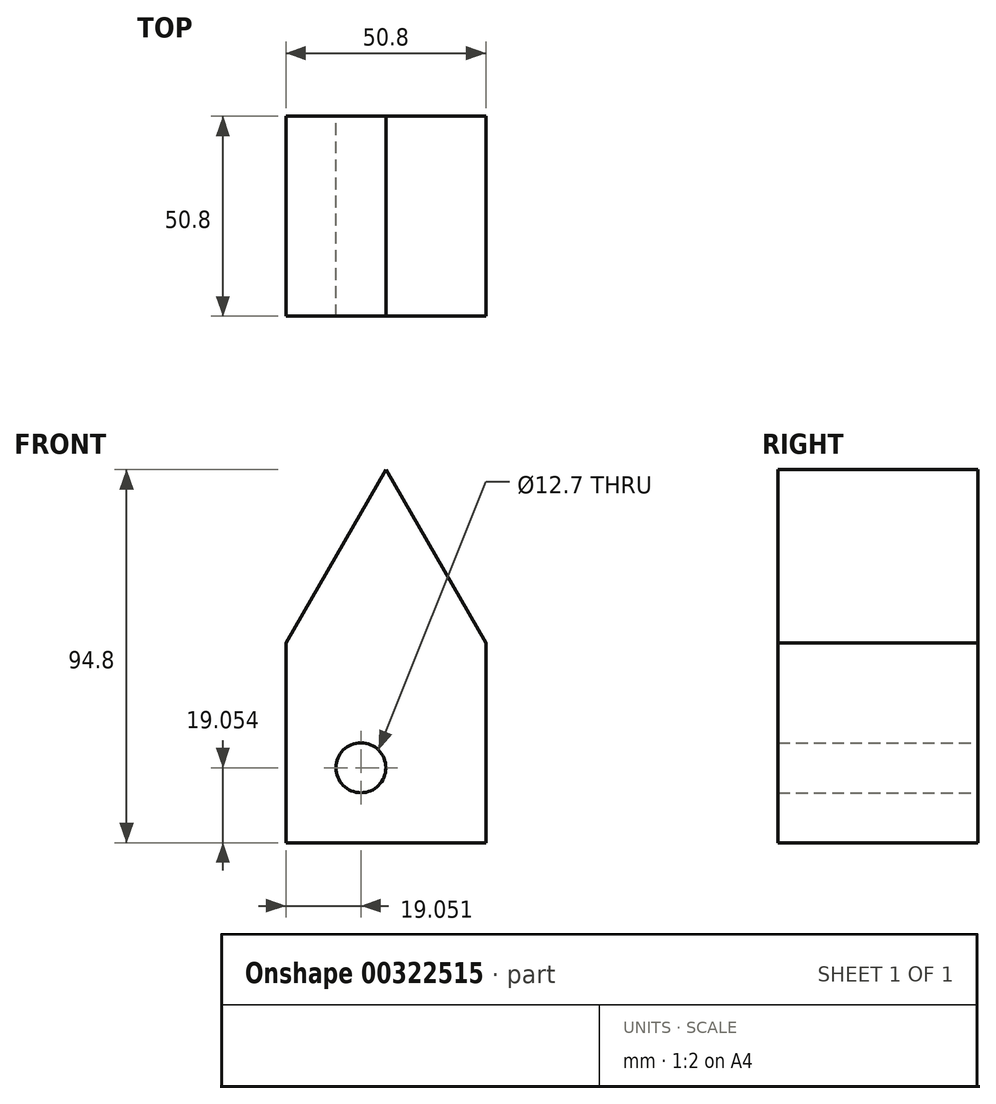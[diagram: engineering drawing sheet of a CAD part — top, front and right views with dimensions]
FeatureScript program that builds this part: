
annotation { "Feature Type Name" : "Feature", "Feature Type Description" : "" }
export const myFeature = defineFeature(function(context is Context, id is Id, definition is map)
    precondition{}
    {
        {
            var Q0;
            Q0=qCreatedBy(makeId("Front.planeOp"),FACE);
            var sketch = newSketch(context, id + "F0", { "sketchPlane" : qUnion([Q0])});
            skLineSegment(sketch, "E0.top", {"start": v(7.1, -41.17) * mm, "end": v(57.9, -41.17) * mm});
            skLineSegment(sketch, "E0.left", {"start": v(7.1, 9.63) * mm, "end": v(7.1, -41.17) * mm});
            skLineSegment(sketch, "E0.right", {"start": v(57.9, 9.63) * mm, "end": v(57.9, -41.17) * mm});
            skLineSegment(sketch, "E1", {"start": v(7.1, 9.63) * mm, "end": v(32.5, 53.63) * mm});
            skLineSegment(sketch, "E2", {"start": v(57.9, 9.63) * mm, "end": v(32.5, 53.63) * mm});
            skCircle(sketch, "E3", {"center": v(26.14, -22.12) * mm, "radius": 6.35 * mm});
            skSolve(sketch);
        }
        {
            var Q0;
            Q0=makeQuery(id+"F0.imprint","IMPRINT",FACE,{"disambiguationData":[TD([[makeQuery(id+"F0.imprint","IMPRINT",EDGE,{"derivedFrom":sQuery(id+"F0.wireOp",EDGE,"E0.top")}),1.0]])]});
            extrude(context, id + "F1", {"entities" : qUnion([Q0]), "depth" : 50.8 * mm});
        }
        {
            var Q0;
            Q0=makeQuery(id+"F0.imprint","IMPRINT",FACE,{"disambiguationData":[TD([[makeQuery(id+"F0.imprint","IMPRINT",EDGE,{"derivedFrom":sQuery(id+"F0.wireOp",EDGE,"E0.top")}),1.0]])]});
            extrude(context, id + "F2", {"entities" : qUnion([Q0]), "operationType" : NewBodyOperationType.ADD, "depth" : 50.8 * mm});
        }
    });
